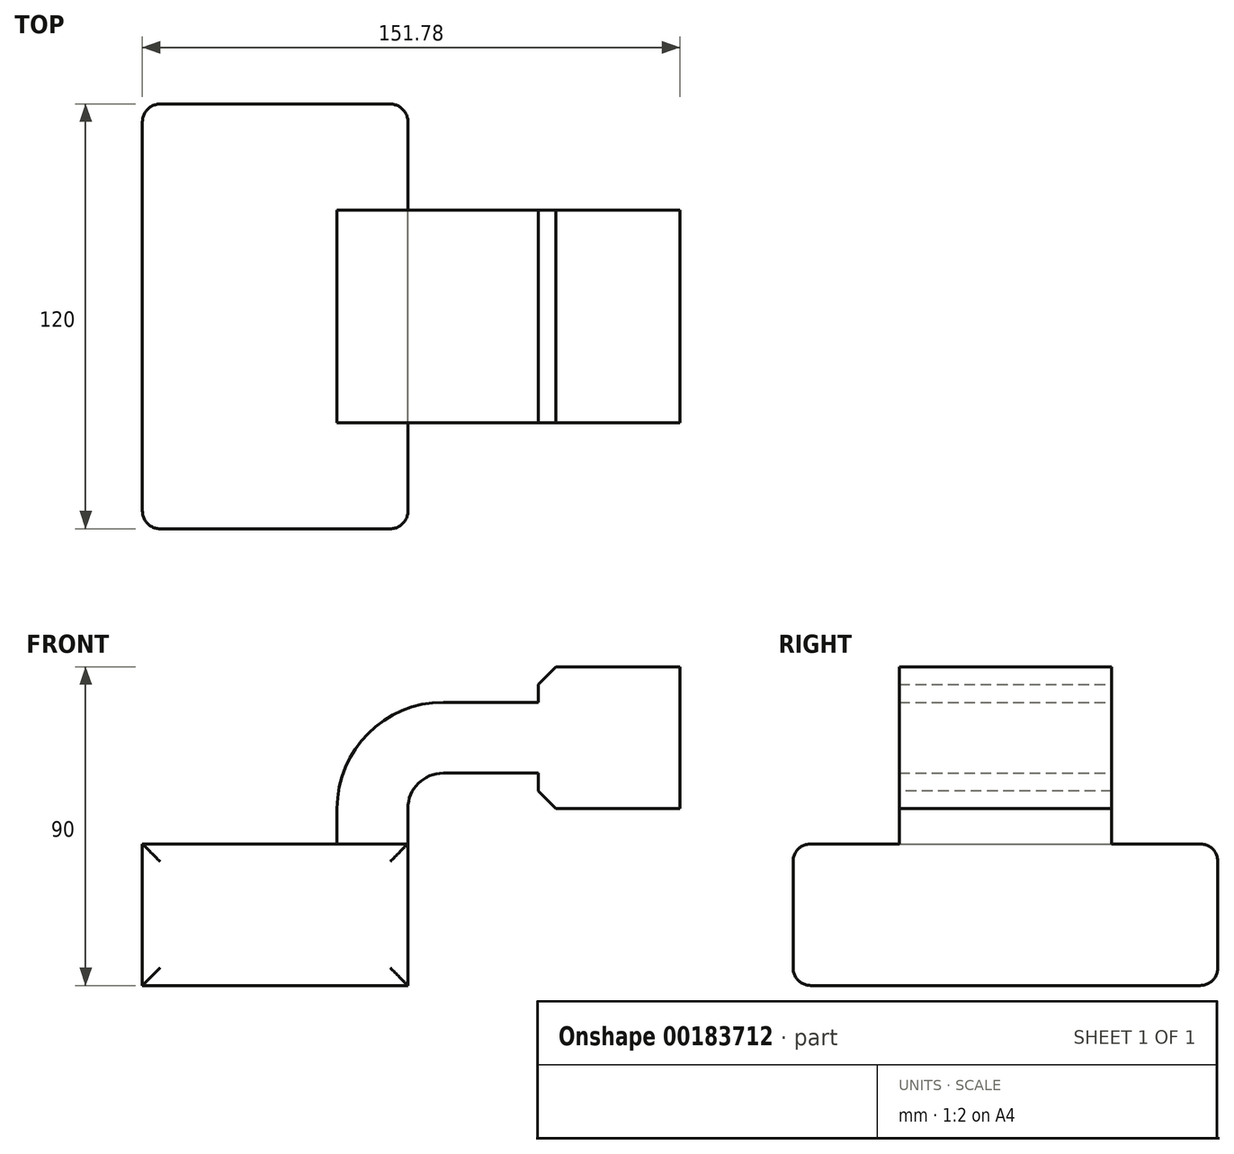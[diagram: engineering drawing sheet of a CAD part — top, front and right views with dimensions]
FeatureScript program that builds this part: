
annotation { "Feature Type Name" : "Feature", "Feature Type Description" : "" }
export const myFeature = defineFeature(function(context is Context, id is Id, definition is map)
    precondition{}
    {
        {
            var Q0;
            Q0=qCreatedBy(makeId("Front.planeOp"),FACE);
            var sketch = newSketch(context, id + "F0", { "sketchPlane" : qUnion([Q0])});
            skLineSegment(sketch, "E0.bottom", {"start": v(37.5, -20) * mm, "end": v(-37.5, -20) * mm});
            skLineSegment(sketch, "E0.top", {"start": v(37.5, 20) * mm, "end": v(-37.5, 20) * mm});
            skLineSegment(sketch, "E0.left", {"start": v(37.5, -20) * mm, "end": v(37.5, 20) * mm});
            skLineSegment(sketch, "E0.right", {"start": v(-37.5, -20) * mm, "end": v(-37.5, 20) * mm});
            skPoint(sketch, "E0.middle", {"position": v(0, 0) * mm});
            skLineSegment(sketch, "E1.bottom", {"start": v(114.28, 30) * mm, "end": v(74.28, 30) * mm});
            skLineSegment(sketch, "E1.top", {"start": v(114.28, 70) * mm, "end": v(74.28, 70) * mm});
            skLineSegment(sketch, "E1.left", {"start": v(114.28, 30) * mm, "end": v(114.28, 70) * mm});
            skLineSegment(sketch, "E1.right", {"start": v(74.28, 30) * mm, "end": v(74.28, 70) * mm});
            skPoint(sketch, "E1.middle", {"position": v(94.28, 50) * mm});
            skLineSegment(sketch, "E2", {"start": v(37.5, 20) * mm, "end": v(37.5, 30) * mm});
            skArc(sketch, "E3", {"start": v(37.5, 30) * mm, "mid": v(40.43, 37.07) * mm, "end": v(47.5, 40) * mm});
            skLineSegment(sketch, "E4", {"start": v(47.5, 40) * mm, "end": v(87.5, 40) * mm});
            skLineSegment(sketch, "E5.0", {"start": v(47.5, 60) * mm, "end": v(87.5, 60) * mm});
            skArc(sketch, "E5.1", {"start": v(17.5, 30) * mm, "mid": v(26.29, 51.21) * mm, "end": v(47.5, 60) * mm});
            skLineSegment(sketch, "E5.2", {"start": v(17.5, 20) * mm, "end": v(17.5, 30) * mm});
            skFitSpline(sketch, "E6", {"points": [v(-37.5, 20) * mm, v(59.46, 60) * mm], "startDerivative": vector(55.23, 106.88) * mm, "endDerivative": vector(119.61, -19.37) * mm});
            skSolve(sketch);
        }
        {
            var Q0;
            {var subQ2=sQuery(id+"F0.wireOp",EDGE,"E2");Q0=makeQuery(id+"F0.imprint","IMPRINT",FACE,{"disambiguationData":[TD([[makeQuery(id+"F0.imprint","IMPRINT",EDGE,{"derivedFrom":subQ2}),1.0]])]});}
            var Q1;
            {var subQ1=sQuery(id+"F0.wireOp",EDGE,"E1.bottom");Q1=makeQuery(id+"F0.imprint","IMPRINT",FACE,{"disambiguationData":[TD([[makeQuery(id+"F0.imprint","IMPRINT",EDGE,{"derivedFrom":subQ1}),-1.0]])]});}
            extrude(context, id + "F1", {"entities" : qUnion([Q0, Q1]), "endBound" : BoundingType.SYMMETRIC, "depth" : 60 * mm});
        }
        {
            var Q0;
            Q0=makeQuery(id+"F0.imprint","IMPRINT",FACE,{"disambiguationData":[TD([[makeQuery(id+"F0.imprint","IMPRINT",EDGE,{"derivedFrom":sQuery(id+"F0.wireOp",EDGE,"E0.bottom")}),-1.0]])]});
            extrude(context, id + "F2", {"entities" : qUnion([Q0]), "operationType" : NewBodyOperationType.ADD, "endBound" : BoundingType.SYMMETRIC, "depth" : 120 * mm});
        }
        {
            var Q0;
            {var subQ0=sQuery(id+"F0.wireOp",EDGE,"E5.1");Q0=makeQuery(id+"F0.imprint","IMPRINT",FACE,{"disambiguationData":[TD([[makeQuery(id+"F0.imprint","IMPRINT",EDGE,{"derivedFrom":subQ0}),1.0]])]});}
            extrude(context, id + "F3", {"entities" : qUnion([Q0]), "operationType" : NewBodyOperationType.ADD, "endBound" : BoundingType.SYMMETRIC, "depth" : 30 * mm});
        }
        {
            var Q0;
            Q0=makeQuery(id+"F2.opExtrude","CAP_EDGE",EDGE,{"disambiguationData":[OSD([sQuery(id+"F0.wireOp",EDGE,"E0.top")])],"isStart":false});
            var Q1;
            Q1=makeQuery(id+"F2.opExtrude","CAP_EDGE",EDGE,{"disambiguationData":[OSD([sQuery(id+"F0.wireOp",EDGE,"E0.right")])],"isStart":false});
            var Q2;
            Q2=makeQuery(id+"F2.opExtrude","CAP_EDGE",EDGE,{"disambiguationData":[OSD([sQuery(id+"F0.wireOp",EDGE,"E0.bottom")])],"isStart":false});
            var Q3;
            Q3=makeQuery(id+"F2.opExtrude","CAP_EDGE",EDGE,{"disambiguationData":[OSD([sQuery(id+"F0.wireOp",EDGE,"E0.left")])],"isStart":false});
            fillet(context, id + "F4", {"entities" : qUnion([Q0, Q1, Q2, Q3]), "radius" : 5 * mm, "tangentPropagation" : true, "allowEdgeOverflow" : false});
        }
        {
            var Q0;
            Q0=makeQuery(id+"F1.opExtrude","SWEPT_EDGE",EDGE,{"disambiguationData":[OSD([sQuery(id+"F0.wireOp",EDGE,"E1.top"),sQuery(id+"F0.wireOp",EDGE,"E1.right")])]});
            var Q1;
            Q1=makeQuery(id+"F1.opExtrude","SWEPT_EDGE",EDGE,{"disambiguationData":[OSD([sQuery(id+"F0.wireOp",EDGE,"E1.bottom"),sQuery(id+"F0.wireOp",EDGE,"E1.right")])]});
            chamfer(context, id + "F5", {"entities" : qUnion([Q0, Q1]), "width" : 5 * mm, "tangentPropagation" : true});
        }
        {
            var Q0;
            Q0=makeQuery(id+"F2.opExtrude","CAP_EDGE",EDGE,{"disambiguationData":[OSD([sQuery(id+"F0.wireOp",EDGE,"E0.top")])],"isStart":true});
            var Q1;
            Q1=makeQuery(id+"F2.opExtrude","CAP_EDGE",EDGE,{"disambiguationData":[OSD([sQuery(id+"F0.wireOp",EDGE,"E0.right")])],"isStart":true});
            var Q2;
            Q2=makeQuery(id+"F2.opExtrude","CAP_EDGE",EDGE,{"disambiguationData":[OSD([sQuery(id+"F0.wireOp",EDGE,"E0.bottom")])],"isStart":true});
            var Q3;
            Q3=makeQuery(id+"F2.opExtrude","CAP_EDGE",EDGE,{"disambiguationData":[OSD([sQuery(id+"F0.wireOp",EDGE,"E0.left")])],"isStart":true});
            fillet(context, id + "F6", {"entities" : qUnion([Q0, Q1, Q2, Q3]), "radius" : 5 * mm, "tangentPropagation" : true, "allowEdgeOverflow" : false});
        }
    });
